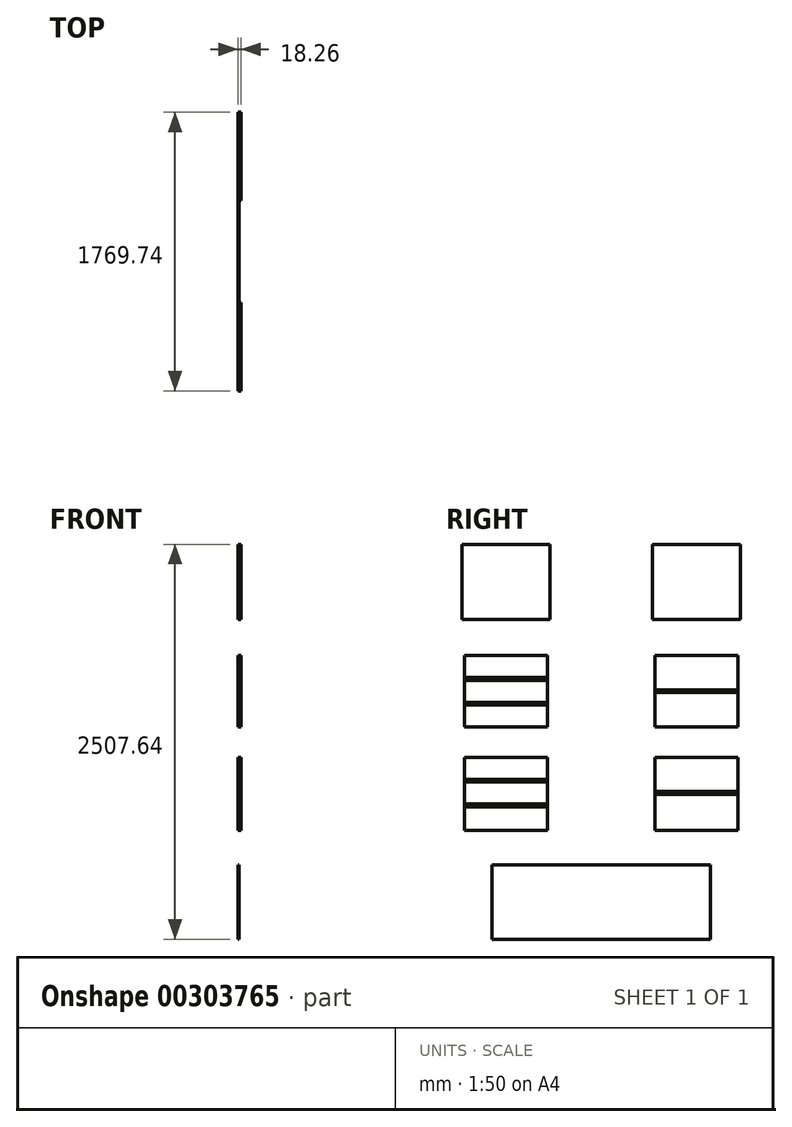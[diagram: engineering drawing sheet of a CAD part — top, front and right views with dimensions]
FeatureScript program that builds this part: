
annotation { "Feature Type Name" : "Feature", "Feature Type Description" : "" }
export const myFeature = defineFeature(function(context is Context, id is Id, definition is map)
    precondition{}
    {
        {
            var Q0;
            Q0=qCreatedBy(makeId("Right.planeOp"),FACE);
            var sketch = newSketch(context, id + "F0", { "sketchPlane" : qUnion([Q0])});
            skLineSegment(sketch, "E0.bottom", {"start": v(-884.87, 932.9) * mm, "end": v(-324.48, 932.9) * mm});
            skLineSegment(sketch, "E0.top", {"start": v(-884.87, 457.45) * mm, "end": v(-324.48, 457.45) * mm});
            skLineSegment(sketch, "E0.left", {"start": v(-884.87, 932.9) * mm, "end": v(-884.87, 457.45) * mm});
            skLineSegment(sketch, "E0.right", {"start": v(-324.48, 932.9) * mm, "end": v(-324.48, 457.45) * mm});
            skPoint(sketch, "E0.middle", {"position": v(-604.67, 695.18) * mm});
            skLineSegment(sketch, "E1.bottom", {"start": v(324.48, 932.9) * mm, "end": v(884.87, 932.9) * mm});
            skLineSegment(sketch, "E1.top", {"start": v(324.48, 457.45) * mm, "end": v(884.87, 457.45) * mm});
            skLineSegment(sketch, "E1.left", {"start": v(324.48, 932.9) * mm, "end": v(324.48, 457.45) * mm});
            skLineSegment(sketch, "E1.right", {"start": v(884.87, 932.9) * mm, "end": v(884.87, 457.45) * mm});
            skPoint(sketch, "E1.middle", {"position": v(604.67, 695.18) * mm});
            skSolve(sketch);
        }
        {
            var Q0;
            Q0=qCreatedBy(makeId("Right.planeOp"),FACE);
            var sketch = newSketch(context, id + "F1", { "sketchPlane" : qUnion([Q0])});
            skLineSegment(sketch, "E2.bottom", {"start": v(867.4, 227.01) * mm, "end": v(341.94, 227.01) * mm});
            skLineSegment(sketch, "E2.top", {"start": v(867.4, -227.01) * mm, "end": v(341.94, -227.01) * mm});
            skLineSegment(sketch, "E2.left", {"start": v(867.4, 227.01) * mm, "end": v(867.4, -227.01) * mm});
            skLineSegment(sketch, "E2.right", {"start": v(341.94, 227.01) * mm, "end": v(341.94, -227.01) * mm});
            skPoint(sketch, "E2.middle", {"position": v(604.67, 0) * mm});
            skLineSegment(sketch, "E3.bottom", {"start": v(-341.94, 227.01) * mm, "end": v(-867.4, 227.01) * mm});
            skLineSegment(sketch, "E3.top", {"start": v(-341.94, -227.01) * mm, "end": v(-867.4, -227.01) * mm});
            skLineSegment(sketch, "E3.left", {"start": v(-341.94, 227.01) * mm, "end": v(-341.94, -227.01) * mm});
            skLineSegment(sketch, "E3.right", {"start": v(-867.4, 227.01) * mm, "end": v(-867.4, -227.01) * mm});
            skPoint(sketch, "E3.middle", {"position": v(-604.67, 0) * mm});
            skLineSegment(sketch, "E4", {"start": v(341.94, 10.32) * mm, "end": v(867.4, 10.32) * mm});
            skLineSegment(sketch, "E5", {"start": v(341.94, -7.94) * mm, "end": v(867.4, -7.94) * mm});
            skLineSegment(sketch, "E6", {"start": v(-867.4, 88.9) * mm, "end": v(-341.94, 88.9) * mm});
            skLineSegment(sketch, "E7", {"start": v(-341.94, 70.64) * mm, "end": v(-867.4, 70.64) * mm});
            skLineSegment(sketch, "E8", {"start": v(-867.4, -69.06) * mm, "end": v(-341.94, -69.06) * mm});
            skLineSegment(sketch, "E9", {"start": v(-341.94, -87.31) * mm, "end": v(-867.4, -87.31) * mm});
            skSolve(sketch);
        }
        {
            var Q0;
            Q0=qCreatedBy(makeId("Right.planeOp"),FACE);
            var sketch = newSketch(context, id + "F2", { "sketchPlane" : qUnion([Q0])});
            skLineSegment(sketch, "E10.bottom", {"start": v(-341.94, -419.46) * mm, "end": v(-867.4, -419.46) * mm});
            skLineSegment(sketch, "E10.top", {"start": v(-341.94, -883) * mm, "end": v(-867.4, -883) * mm});
            skLineSegment(sketch, "E10.left", {"start": v(-341.94, -419.46) * mm, "end": v(-341.94, -883) * mm});
            skLineSegment(sketch, "E10.right", {"start": v(-867.4, -419.46) * mm, "end": v(-867.4, -883) * mm});
            skPoint(sketch, "E10.middle", {"position": v(-604.67, -651.23) * mm});
            skLineSegment(sketch, "E11.bottom", {"start": v(867.4, -419.46) * mm, "end": v(341.94, -419.46) * mm});
            skLineSegment(sketch, "E11.top", {"start": v(867.4, -883) * mm, "end": v(341.94, -883) * mm});
            skLineSegment(sketch, "E11.left", {"start": v(867.4, -419.46) * mm, "end": v(867.4, -883) * mm});
            skLineSegment(sketch, "E11.right", {"start": v(341.94, -419.46) * mm, "end": v(341.94, -883) * mm});
            skPoint(sketch, "E11.middle", {"position": v(604.67, -651.23) * mm});
            skLineSegment(sketch, "E12", {"start": v(-867.4, -557.97) * mm, "end": v(-341.94, -557.97) * mm});
            skLineSegment(sketch, "E13", {"start": v(-867.4, -576.22) * mm, "end": v(-341.94, -576.22) * mm});
            skLineSegment(sketch, "E14", {"start": v(-867.4, -715.92) * mm, "end": v(-341.94, -715.92) * mm});
            skLineSegment(sketch, "E15", {"start": v(-867.4, -734.18) * mm, "end": v(-341.94, -734.18) * mm});
            skLineSegment(sketch, "E16", {"start": v(341.94, -636.55) * mm, "end": v(867.4, -636.55) * mm});
            skLineSegment(sketch, "E17", {"start": v(867.4, -654.8) * mm, "end": v(341.94, -654.8) * mm});
            skSolve(sketch);
        }
        {
            var Q0;
            Q0=qCreatedBy(makeId("Right.planeOp"),FACE);
            var sketch = newSketch(context, id + "F3", { "sketchPlane" : qUnion([Q0])});
            skLineSegment(sketch, "E18.bottom", {"start": v(694.53, -1102.46) * mm, "end": v(-694.53, -1102.46) * mm});
            skLineSegment(sketch, "E18.top", {"start": v(694.53, -1574.74) * mm, "end": v(-694.53, -1574.74) * mm});
            skLineSegment(sketch, "E18.left", {"start": v(694.53, -1102.46) * mm, "end": v(694.53, -1574.74) * mm});
            skLineSegment(sketch, "E18.right", {"start": v(-694.53, -1102.46) * mm, "end": v(-694.53, -1574.74) * mm});
            skPoint(sketch, "E18.middle", {"position": v(0, -1338.6) * mm});
            skSolve(sketch);
        }
        {
            var Q0;
            Q0=makeQuery(id+"F0.imprint","IMPRINT",FACE,{"disambiguationData":[TD([[makeQuery(id+"F0.imprint","IMPRINT",EDGE,{"derivedFrom":sQuery(id+"F0.wireOp",EDGE,"E0.bottom")}),-1.0]])]});
            var Q1;
            Q1=makeQuery(id+"F0.imprint","IMPRINT",FACE,{"disambiguationData":[TD([[makeQuery(id+"F0.imprint","IMPRINT",EDGE,{"derivedFrom":sQuery(id+"F0.wireOp",EDGE,"E1.bottom")}),-1.0]])]});
            var Q2;
            {var subQ0=sQuery(id+"F1.wireOp",EDGE,"E2.bottom");Q2=makeQuery(id+"F1.imprint","IMPRINT",FACE,{"disambiguationData":[TD([[makeQuery(id+"F1.imprint","IMPRINT",EDGE,{"derivedFrom":subQ0}),1.0]])]});}
            var Q3;
            {var subQ0=sQuery(id+"F1.wireOp",EDGE,"E2.top");Q3=makeQuery(id+"F1.imprint","IMPRINT",FACE,{"disambiguationData":[TD([[makeQuery(id+"F1.imprint","IMPRINT",EDGE,{"derivedFrom":subQ0}),-1.0]])]});}
            var Q4;
            {var subQ0=sQuery(id+"F1.wireOp",EDGE,"E3.bottom");Q4=makeQuery(id+"F1.imprint","IMPRINT",FACE,{"disambiguationData":[TD([[makeQuery(id+"F1.imprint","IMPRINT",EDGE,{"derivedFrom":subQ0}),1.0]])]});}
            var Q5;
            {var subQ0=sQuery(id+"F1.wireOp",EDGE,"E7");Q5=makeQuery(id+"F1.imprint","IMPRINT",FACE,{"disambiguationData":[TD([[makeQuery(id+"F1.imprint","IMPRINT",EDGE,{"derivedFrom":subQ0}),1.0]])]});}
            var Q6;
            {var subQ0=sQuery(id+"F1.wireOp",EDGE,"E3.top");Q6=makeQuery(id+"F1.imprint","IMPRINT",FACE,{"disambiguationData":[TD([[makeQuery(id+"F1.imprint","IMPRINT",EDGE,{"derivedFrom":subQ0}),-1.0]])]});}
            var Q7;
            {var subQ0=sQuery(id+"F2.wireOp",EDGE,"E10.bottom");Q7=makeQuery(id+"F2.imprint","IMPRINT",FACE,{"disambiguationData":[TD([[makeQuery(id+"F2.imprint","IMPRINT",EDGE,{"derivedFrom":subQ0}),1.0]])]});}
            var Q8;
            {var subQ0=sQuery(id+"F2.wireOp",EDGE,"E13");Q8=makeQuery(id+"F2.imprint","IMPRINT",FACE,{"disambiguationData":[TD([[makeQuery(id+"F2.imprint","IMPRINT",EDGE,{"derivedFrom":subQ0}),-1.0]])]});}
            var Q9;
            {var subQ0=sQuery(id+"F2.wireOp",EDGE,"E10.top");Q9=makeQuery(id+"F2.imprint","IMPRINT",FACE,{"disambiguationData":[TD([[makeQuery(id+"F2.imprint","IMPRINT",EDGE,{"derivedFrom":subQ0}),-1.0]])]});}
            var Q10;
            {var subQ0=sQuery(id+"F2.wireOp",EDGE,"E11.bottom");Q10=makeQuery(id+"F2.imprint","IMPRINT",FACE,{"disambiguationData":[TD([[makeQuery(id+"F2.imprint","IMPRINT",EDGE,{"derivedFrom":subQ0}),1.0]])]});}
            var Q11;
            {var subQ0=sQuery(id+"F2.wireOp",EDGE,"E11.top");Q11=makeQuery(id+"F2.imprint","IMPRINT",FACE,{"disambiguationData":[TD([[makeQuery(id+"F2.imprint","IMPRINT",EDGE,{"derivedFrom":subQ0}),-1.0]])]});}
            extrude(context, id + "F4", {"entities" : qUnion([Q0, Q1, Q2, Q3, Q4, Q5, Q6, Q7, Q8, Q9, Q10, Q11]), "depth" : 18.26 * mm, "offsetDistance" : 25.4 * mm});
        }
        {
            var Q0;
            {var subQ0=sQuery(id+"F1.wireOp",EDGE,"E6");Q0=makeQuery(id+"F1.imprint","IMPRINT",FACE,{"disambiguationData":[TD([[makeQuery(id+"F1.imprint","IMPRINT",EDGE,{"derivedFrom":subQ0}),-1.0]])]});}
            var Q1;
            {var subQ0=sQuery(id+"F1.wireOp",EDGE,"E8");Q1=makeQuery(id+"F1.imprint","IMPRINT",FACE,{"disambiguationData":[TD([[makeQuery(id+"F1.imprint","IMPRINT",EDGE,{"derivedFrom":subQ0}),-1.0]])]});}
            var Q2;
            {var subQ0=sQuery(id+"F2.wireOp",EDGE,"E12");Q2=makeQuery(id+"F2.imprint","IMPRINT",FACE,{"disambiguationData":[TD([[makeQuery(id+"F2.imprint","IMPRINT",EDGE,{"derivedFrom":subQ0}),-1.0]])]});}
            var Q3;
            {var subQ0=sQuery(id+"F2.wireOp",EDGE,"E14");Q3=makeQuery(id+"F2.imprint","IMPRINT",FACE,{"disambiguationData":[TD([[makeQuery(id+"F2.imprint","IMPRINT",EDGE,{"derivedFrom":subQ0}),-1.0]])]});}
            var Q4;
            {var subQ0=sQuery(id+"F2.wireOp",EDGE,"E16");Q4=makeQuery(id+"F2.imprint","IMPRINT",FACE,{"disambiguationData":[TD([[makeQuery(id+"F2.imprint","IMPRINT",EDGE,{"derivedFrom":subQ0}),-1.0]])]});}
            var Q5;
            {var subQ0=sQuery(id+"F1.wireOp",EDGE,"E4");Q5=makeQuery(id+"F1.imprint","IMPRINT",FACE,{"disambiguationData":[TD([[makeQuery(id+"F1.imprint","IMPRINT",EDGE,{"derivedFrom":subQ0}),-1.0]])]});}
            extrude(context, id + "F5", {"entities" : qUnion([Q0, Q1, Q2, Q3, Q4, Q5]), "operationType" : NewBodyOperationType.ADD, "depth" : (3 / 4 - (7 / 8 / 2)) * mm, "offsetDistance" : 25.4 * mm});
        }
        {
            var Q0;
            Q0=makeQuery(id+"F3.imprint","IMPRINT",FACE,{"disambiguationData":[TD([[makeQuery(id+"F3.imprint","IMPRINT",EDGE,{"derivedFrom":sQuery(id+"F3.wireOp",EDGE,"E18.bottom")}),1.0]])]});
            extrude(context, id + "F6", {"entities" : qUnion([Q0]), "depth" : 6.35 * mm, "offsetDistance" : 25.4 * mm});
        }
    });
